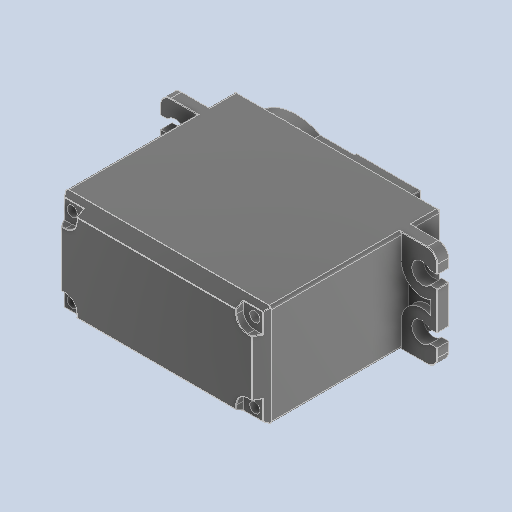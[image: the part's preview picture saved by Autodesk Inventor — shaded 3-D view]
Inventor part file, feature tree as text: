
AUTODESK INVENTOR PART (.ipt)
format: ipt  version: 2025.1 (Build 291241000, 241)  size: 509,952 bytes
history: native  units: mm
features: fillet x1
ambient origin geometry x8: Origin, YZ Plane, XZ Plane, XY Plane, X Axis, Y Axis, Z Axis, Center Point
bodies: Volumenkörper1 (feature_tree)
feature tree (1):
  fillet  "Fillet8"  [1 undecoded]
note: 1 required parameter value undecoded (feature->parameter linkage not recoverable at this tier; creation-order binding heuristic only, values carry confidence <= 0.55)
